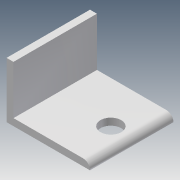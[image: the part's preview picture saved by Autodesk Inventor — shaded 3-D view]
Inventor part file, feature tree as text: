
AUTODESK INVENTOR PART (.ipt)
format: ipt  version: 2014 (Build 180170000, 170)  size: 96,768 bytes
history: native  units: in
note: dims shown in document units (in); Inventor stores cm internally (conversion verified against a paired STEP export)
features: extrude x3, sketch x3
ambient origin geometry x8: Origin, YZ Plane, XZ Plane, XY Plane, X Axis, Y Axis, Z Axis, Center Point
bodies: Solid1 (feature_tree)
feature tree (6):
  extrude  "Extrusion1"  Depth=1.5in
  extrude  "Extrusion2"  Depth=1.5in TaperAngle=0.0deg
  extrude  "Extrusion3"  Depth=1.0in
  sketch  "Sketch1"  dims[d0=1.5in d1=1.5in]
  sketch  "Sketch2"  dims[d2=0.125in d3=1.5in d4=0.0in]
  sketch  "Sketch3"  dims[d5=0.375in d6=0.375in d7=1.5in d8=0.0in d9=0.5in d10=1.0in d11=0.0in]
